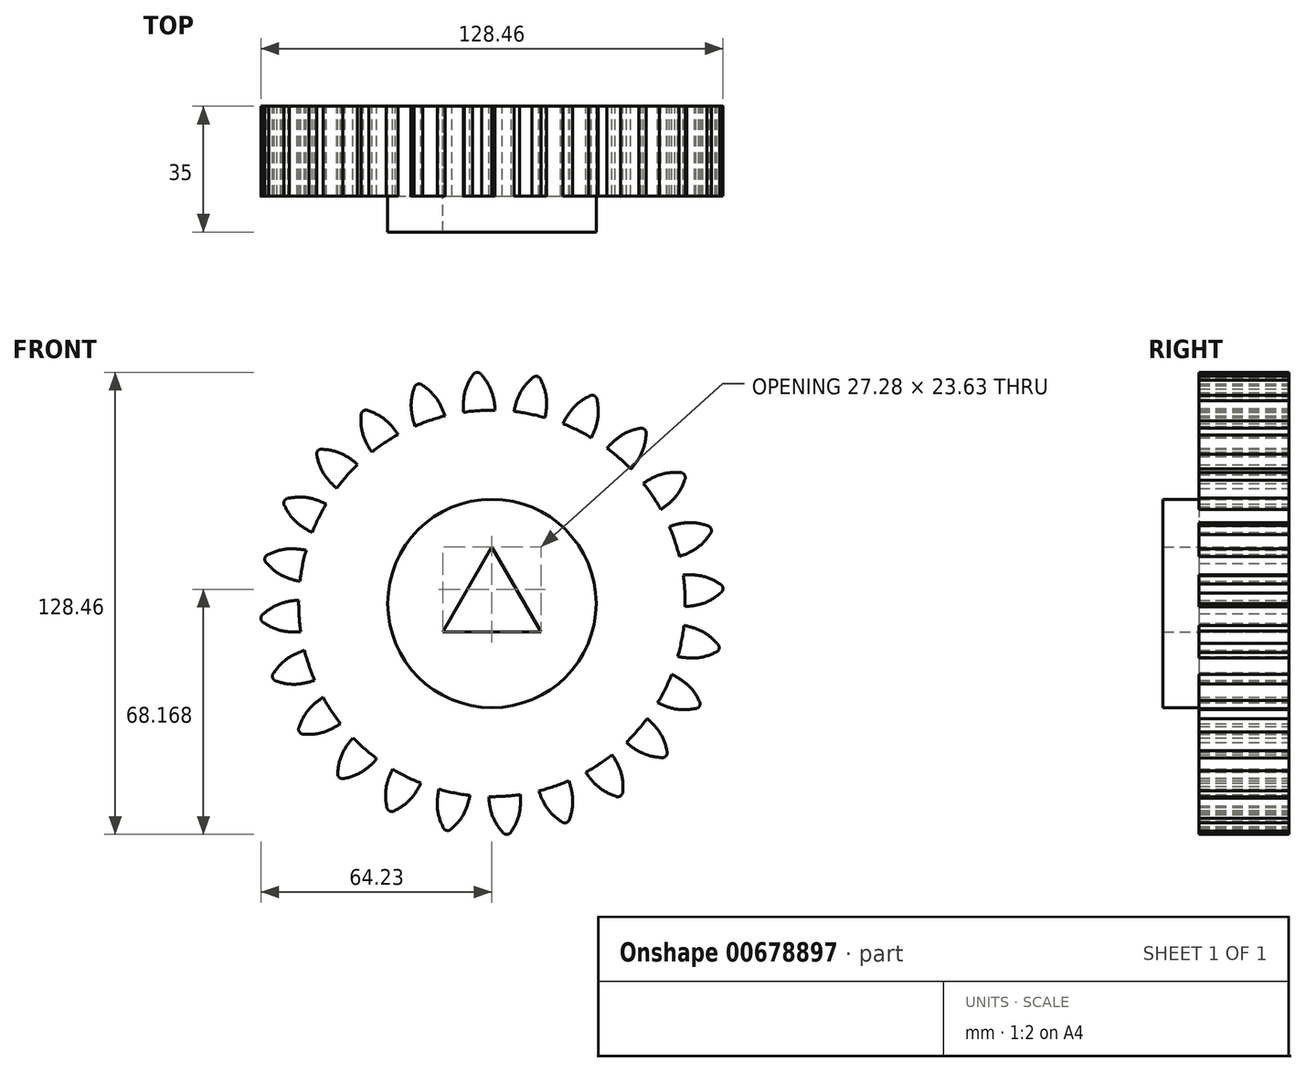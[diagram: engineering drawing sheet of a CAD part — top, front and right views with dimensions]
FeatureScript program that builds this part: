
annotation { "Feature Type Name" : "Feature", "Feature Type Description" : "" }
export const myFeature = defineFeature(function(context is Context, id is Id, definition is map)
    precondition{}
    {
        {
            var Q0;
            Q0=qCreatedBy(makeId("Front.planeOp"),FACE);
            var sketch = newSketch(context, id + "F0", { "sketchPlane" : qUnion([Q0])});
            skCircle(sketch, "E0", {"center": v(0, 0) * mm, "radius": 53.72 * mm});
            skCircle(sketch, "E1", {"center": v(0, 0) * mm, "radius": 63.5 * mm, "construction": true});
            skCircle(sketch, "E2", {"center": v(0, 0) * mm, "radius": 58.67 * mm, "construction": true});
            skLineSegment(sketch, "E3", {"start": v(0, 0) * mm, "end": v(0, 73.73) * mm, "construction": true});
            skLineSegment(sketch, "E4", {"start": v(0, 0) * mm, "end": v(-5.07, 77.32) * mm, "construction": true});
            skLineSegment(sketch, "E5", {"start": v(0, 58.67) * mm, "end": v(-93.6, 58.67) * mm, "construction": true});
            skLineSegment(sketch, "E6", {"start": v(0, 58.67) * mm, "end": v(-94.94, 24.12) * mm, "construction": true});
            skCircle(sketch, "E7", {"center": v(-13.72, 53.68) * mm, "radius": 14.6 * mm, "construction": true});
            skCircle(sketch, "E8", {"center": v(0, 0) * mm, "radius": 55.14 * mm, "construction": true});
            skArc(sketch, "E9", {"start": v(0, 58.67) * mm, "mid": v(-1.2, 61.2) * mm, "end": v(-2.86, 63.44) * mm});
            skArc(sketch, "E10", {"start": v(0.88, 53.71) * mm, "mid": v(0.6, 56.22) * mm, "end": v(0, 58.67) * mm});
            skArc(sketch, "E11.MirrorCS", {"start": v(-7.88, 53.14) * mm, "mid": v(-7.93, 55.66) * mm, "end": v(-7.66, 58.17) * mm});
            skCircle(sketch, "E12.MirrorC", {"center": v(6.6, 55.01) * mm, "radius": 14.6 * mm, "construction": true});
            skArc(sketch, "E13", {"start": v(-5.45, 63.27) * mm, "mid": v(-6.83, 60.84) * mm, "end": v(-7.66, 58.17) * mm});
            skArc(sketch, "E14", {"start": v(-2.86, 63.44) * mm, "mid": v(-4.2, 64.22) * mm, "end": v(-5.45, 63.27) * mm});
            skCircle(sketch, "E15", {"center": v(0, 0) * mm, "radius": 28.97 * mm});
            skCircle(sketch, "E16.cCircle", {"center": v(0, 0) * mm, "radius": 15.75 * mm, "construction": true});
            skLineSegment(sketch, "E16.0", {"start": v(0, 15.75) * mm, "end": v(13.64, -7.88) * mm});
            skLineSegment(sketch, "E16.1", {"start": v(13.64, -7.88) * mm, "end": v(-13.64, -7.88) * mm});
            skLineSegment(sketch, "E16.2", {"start": v(-13.64, -7.88) * mm, "end": v(0, 15.75) * mm});
            skSolve(sketch);
        }
        {
            var Q0;
            {var subQ0=sQuery(id+"F0.wireOp",EDGE,"E0");var subQ1=makeQuery(id+"F0.imprint","INTERSECT",VERTEX,{"derivedFrom":[subQ0,sQuery(id+"F0.wireOp",EDGE,"E10")]});Q0=makeQuery(id+"F0.imprint","IMPRINT",FACE,{"disambiguationData":[TD([[makeQuery(id+"F0.imprint","IMPRINT",EDGE,{"disambiguationData":[TD([[subQ1,1.0]])],"derivedFrom":subQ0}),-1.0]])]});}
            var Q1;
            Q1=makeQuery(id+"F0.imprint","IMPRINT",FACE,{"disambiguationData":[TD([[makeQuery(id+"F0.imprint","IMPRINT",EDGE,{"derivedFrom":sQuery(id+"F0.wireOp",EDGE,"E9")}),1.0]])]});
            extrude(context, id + "F1", {"entities" : qUnion([Q0, Q1]), "depth" : 25 * mm, "offsetDistance" : 25 * mm});
        }
        {
            var Q0;
            Q0=makeQuery(id+"F1.opExtrude","SWEPT_BODY",BODY,{"disambiguationData":[OSD([sQuery(id+"F0.wireOp",EDGE,"E0"),sQuery(id+"F0.wireOp",EDGE,"E9"),sQuery(id+"F0.wireOp",EDGE,"E10"),sQuery(id+"F0.wireOp",EDGE,"E11.MirrorCS"),sQuery(id+"F0.wireOp",EDGE,"E13"),sQuery(id+"F0.wireOp",EDGE,"E14")])]});
            var Q1;
            Q1=makeQuery(id+"F1.opExtrude","SWEPT_FACE",FACE,{"disambiguationData":[OSD([sQuery(id+"F0.wireOp",EDGE,"E0")])]});
            circularPattern(context, id + "F2", {"entities" : qUnion([Q0]), "axis" : qUnion([Q1]), "angle" : 360 * degree, "instanceCount" : 24, "equalSpace" : true});
        }
        {
            var Q0;
            Q0=makeQuery(id+"F0.imprint","IMPRINT",FACE,{"disambiguationData":[TD([[makeQuery(id+"F0.imprint","IMPRINT",EDGE,{"derivedFrom":sQuery(id+"F0.wireOp",EDGE,"E15")}),1.0]])]});
            extrude(context, id + "F3", {"entities" : qUnion([Q0]), "operationType" : NewBodyOperationType.ADD, "depth" : 35 * mm, "offsetDistance" : 25 * mm});
        }
    });
